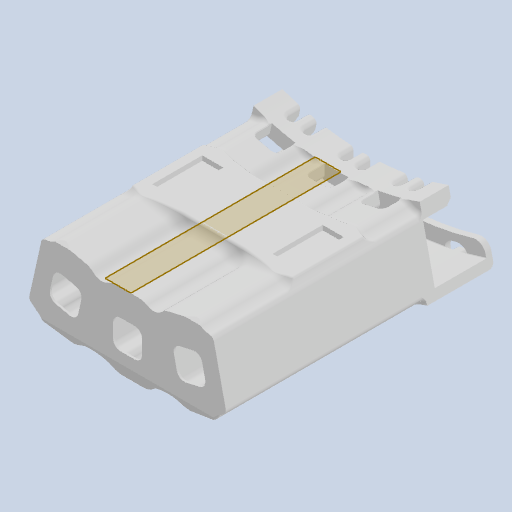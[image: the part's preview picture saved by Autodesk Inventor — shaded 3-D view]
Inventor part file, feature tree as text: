
AUTODESK INVENTOR PART (.ipt)
format: ipt  version: 2022 (Build 260153000, 153)  size: 2,992,640 bytes
history: native  units: mm
features: projected_geometry x44, reference x32, fillet x27, extrude x24, sketch x24, other x10, chamfer x1
ambient origin geometry x8: Origin, YZ Plane, XZ Plane, XY Plane, X Axis, Y Axis, Z Axis, Center Point
bodies: Body1 (feature_tree)
feature tree (162):
  other  "Твердое тело1"
  extrude  "Выдавливание1"  Depth=1.0mm
  extrude  "Выдавливание2"  Depth=1.0mm
  fillet  "Сопряжение5"  Radius=1.0mm
  fillet  "Сопряжение6"  Radius=1.0mm
  extrude  "Выдавливание6"  Depth=43.0mm TaperAngle=0.0deg
  sketch  "Эскиз8"
  sketch  "Эскиз9"
  extrude  "Выдавливание7"  Depth=0.4mm TaperAngle=0.0deg
  extrude  "Выдавливание8"  Depth=1.0mm
  extrude  "Выдавливание9"  Depth=6.0mm
  extrude  "Выдавливание10"  Depth=6.0mm
  fillet  "Сопряжение7"  Radius=6.0mm
  fillet  "Сопряжение8"  Radius=6.0mm
  fillet  "Сопряжение9"  Radius=6.0mm
  fillet  "Сопряжение10"  Radius=6.0mm
  extrude  "Выдавливание11"  Depth=1.5mm
  extrude  "Выдавливание12"  Depth=5.0mm
  extrude  "Выдавливание13"  Depth=49.0mm TaperAngle=0.0deg
  extrude  "Выдавливание14"  Depth=5.0mm
  extrude  "Выдавливание15"  Depth=5.0mm
  extrude  "Выдавливание16"  Depth=49.0mm TaperAngle=0.0deg
  fillet  "Сопряжение11"  Radius=49.0mm
  fillet  "Сопряжение12"  Radius=2.0mm
  fillet  "Сопряжение13"  Radius=2.0mm
  fillet  "Сопряжение14"  Radius=2.0mm
  fillet  "Сопряжение15"  Radius=2.0mm
  fillet  "Сопряжение16"  Radius=2.0mm
  fillet  "Сопряжение20"  Radius=2.0mm
  fillet  "Сопряжение21"  Radius=1.0mm
  chamfer  "Фаска1"  Distance=1.0mm
  extrude  "Выдавливание22"  Depth=1.0mm
  extrude  "Выдавливание23"  Depth=1.0mm
  fillet  "Сопряжение24"  Radius=1.0mm
  fillet  "Сопряжение25"  Radius=1.0mm
  fillet  "Сопряжение26"  Radius=49.0mm
  fillet  "Сопряжение27"  Radius=43.0mm
  extrude  "Выдавливание24"  Depth=4.0mm
  fillet  "Сопряжение28"  Radius=2.5mm
  fillet  "Сопряжение29"  Radius=3.0mm
  fillet  "Сопряжение30"  Radius=1.0mm
  fillet  "Сопряжение31"  Radius=2.0mm
  fillet  "Сопряжение32"  Radius=10.7mm
  extrude  "Выдавливание27"  Depth=3.0mm
  extrude  "Выдавливание28"  Depth=1.2mm TaperAngle=0.0deg
  extrude  "Выдавливание29"  Depth=2.0mm
  fillet  "Сопряжение35"  Radius=6.0mm
  other  "РабПлоскость3"
  extrude  "Выдавливание30"  Depth=2.0mm TaperAngle=0.0deg
  extrude  "Выдавливание31"  Depth=2.0mm TaperAngle=0.0deg
  extrude  "Выдавливание32"  Depth=5.0mm
  extrude  "Выдавливание33"  Depth=4.0mm
  fillet  "Сопряжение36"  Radius=50.0mm
  fillet  "Сопряжение37"  Radius=5.0mm
  fillet  "Сопряжение38"  Radius=4.0mm
  extrude  "Выдавливание34"  Depth=50.0mm TaperAngle=0.0deg
  sketch  "Эскиз1"
  reference  "Ссылка1"
  reference  "Ссылка2"
  reference  "Ссылка3"
  reference  "Ссылка4"
  reference  "Ссылка5"
  reference  "Ссылка6"
  reference  "Ссылка7"
  reference  "Ссылка8"
  reference  "Ссылка9"
  reference  "Ссылка10"
  reference  "Ссылка11"
  reference  "Ссылка12"
  reference  "Ссылка13"
  sketch  "Эскиз2"
  projected_geometry  "Спроецированная петля1"
  sketch  "Эскиз7"
  projected_geometry  "Спроецированная петля4"
  projected_geometry  "Спроецированная петля5"
  projected_geometry  "Спроецированная петля6"
  projected_geometry  "Спроецированная петля7"
  sketch  "Эскиз10"
  projected_geometry  "Спроецированная петля8"
  projected_geometry  "Спроецированная петля9"
  projected_geometry  "Спроецированная петля10"
  projected_geometry  "Спроецированная петля11"
  sketch  "Эскиз11"
  projected_geometry  "Спроецированная петля12"
  sketch  "Эскиз12"
  projected_geometry  "Спроецированная петля13"
  projected_geometry  "Спроецированная петля14"
  reference  "Ссылка14"
  reference  "Ссылка15"
  reference  "Ссылка16"
  reference  "Ссылка17"
  reference  "Ссылка18"
  reference  "Ссылка19"
  reference  "Ссылка20"
  reference  "Ссылка21"
  reference  "Ссылка22"
  reference  "Ссылка23"
  reference  "Ссылка24"
  reference  "Ссылка25"
  reference  "Ссылка26"
  sketch  "Эскиз13"
  projected_geometry  "Спроецированная петля15"
  sketch  "Эскиз14"
  projected_geometry  "Спроецированная петля16"
  reference  "Ссылка27"
  reference  "Ссылка28"
  sketch  "Эскиз15"
  projected_geometry  "Спроецированная петля17"
  sketch  "Эскиз16"
  projected_geometry  "Спроецированная петля18"
  sketch  "Эскиз17"
  projected_geometry  "Спроецированная петля19"
  sketch  "Эскиз24"
  projected_geometry  "Спроецированная петля24"
  projected_geometry  "Спроецированная петля25"
  projected_geometry  "Спроецированная петля26"
  projected_geometry  "Спроецированная петля27"
  projected_geometry  "Спроецированная петля29"
  projected_geometry  "Спроецированная петля30"
  projected_geometry  "Спроецированная петля31"
  projected_geometry  "Спроецированная петля32"
  projected_geometry  "Спроецированная петля33"
  sketch  "Эскиз25"
  sketch  "Эскиз26"
  projected_geometry  "Спроецированная петля40"
  projected_geometry  "Спроецированная петля41"
  projected_geometry  "Спроецированная петля42"
  projected_geometry  "Спроецированная петля43"
  projected_geometry  "Спроецированная петля44"
  reference  "Ссылка29"
  projected_geometry  "Спроецированная петля45"
  projected_geometry  "Спроецированная петля46"
  projected_geometry  "Спроецированная петля47"
  sketch  "Эскиз30"
  reference  "Ссылка31"
  projected_geometry  "Спроецированная петля50"
  reference  "Ссылка32"
  sketch  "Эскиз31"
  projected_geometry  "Спроецированная петля51"
  sketch  "Эскиз32"
  projected_geometry  "Спроецированная петля52"
  sketch  "Эскиз35"
  projected_geometry  "Спроецированная петля56"
  projected_geometry  "Спроецированная петля57"
  projected_geometry  "Спроецированная петля58"
  sketch  "Эскиз36"
  projected_geometry  "Спроецированная петля59"
  sketch  "Эскиз37"
  projected_geometry  "Спроецированная петля60"
  projected_geometry  "Спроецированная петля61"
  sketch  "Эскиз38"
  projected_geometry  "Спроецированная петля62"
  sketch  "Эскиз39"
  reference  "Ссылка33"
  other  "<userpath>\Documents\Git\MZCAT_2024\MZCAT_2.iam"
  other  "MZCAT_2.iam"
  other  "vydacha_chertezh:1"
  other  "sensors_frame:1"
  other  "CAT_protector:1"
  other  "<userpath>\Documents\Git\MZCAT_2024\MZCAT_4.iam"
  other  "MZCAT_4.iam"
  other  "magazine_fixator:1"
